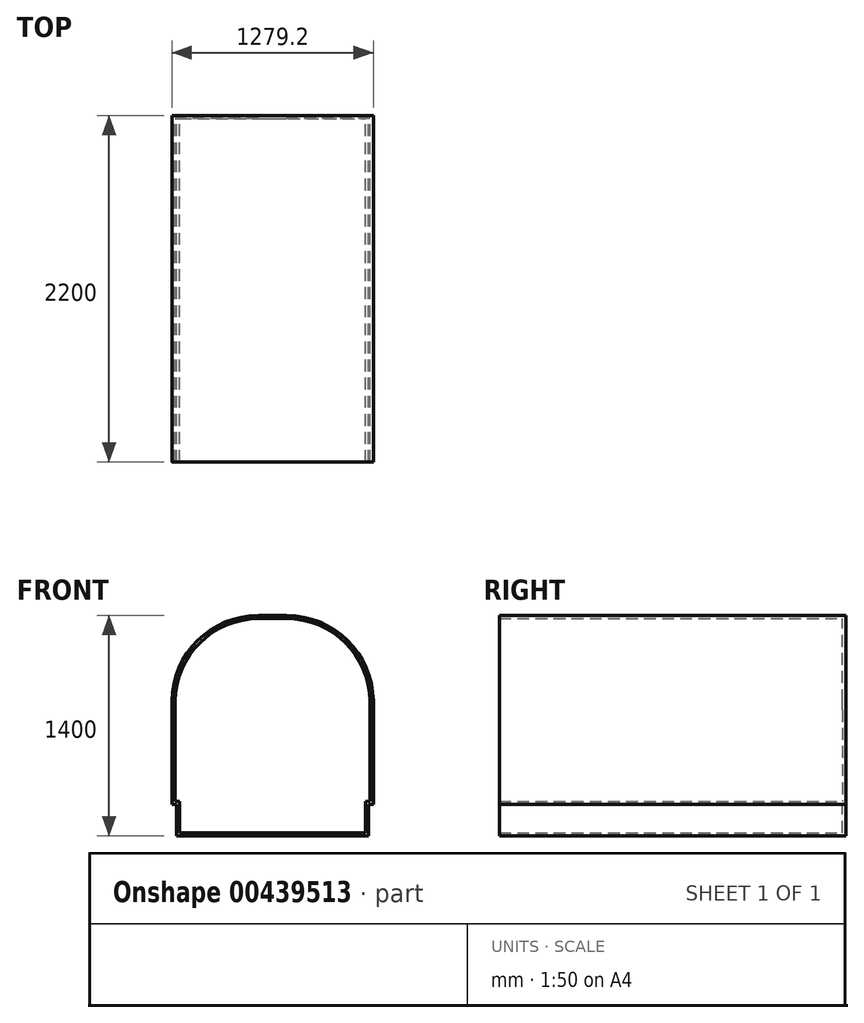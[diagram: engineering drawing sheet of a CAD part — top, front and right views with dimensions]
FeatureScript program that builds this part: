
annotation { "Feature Type Name" : "Feature", "Feature Type Description" : "" }
export const myFeature = defineFeature(function(context is Context, id is Id, definition is map)
    precondition{}
    {
        {
            var Q0;
            Q0=qCreatedBy(makeId("Front.planeOp"),FACE);
            var sketch = newSketch(context, id + "F0", { "sketchPlane" : qUnion([Q0])});
            skLineSegment(sketch, "E0", {"start": v(-609.6, 0) * mm, "end": v(609.6, 0) * mm});
            skLineSegment(sketch, "E1", {"start": v(-609.6, 0) * mm, "end": v(-609.6, 300) * mm});
            skLineSegment(sketch, "E2", {"start": v(609.6, 0) * mm, "end": v(609.6, 300) * mm});
            skLineSegment(sketch, "E3", {"start": v(-609.6, 300) * mm, "end": v(609.6, 300) * mm, "construction": true});
            skLineSegment(sketch, "E4", {"start": v(-89.29, 1400) * mm, "end": v(89.29, 1400) * mm});
            skLineSegment(sketch, "E5", {"start": v(0, 0) * mm, "end": v(0, 1400) * mm, "construction": true});
            skLineSegment(sketch, "E6", {"start": v(-1109.6, 300) * mm, "end": v(-309.6, 300) * mm, "construction": true});
            skLineSegment(sketch, "E7", {"start": v(-639.6, 800) * mm, "end": v(-639.6, 200) * mm});
            skLineSegment(sketch, "E8.MirrorCS", {"start": v(639.6, 800) * mm, "end": v(639.6, 200) * mm});
            skArc(sketch, "E9", {"start": v(-639.6, 800) * mm, "mid": v(-639.51, 828.42) * mm, "end": v(-639.25, 856.85) * mm});
            skArc(sketch, "E10", {"start": v(639.6, 800) * mm, "mid": v(639.51, 828.42) * mm, "end": v(639.25, 856.85) * mm});
            skPoint(sketch, "E11.visualSharp", {"position": v(-600, 1400) * mm});
            skArc(sketch, "E11.filletArc", {"start": v(-89.29, 1400) * mm, "mid": v(-475.77, 1241.32) * mm, "end": v(-639.25, 856.85) * mm});
            skPoint(sketch, "E12.visualSharp", {"position": v(600, 1400) * mm});
            skArc(sketch, "E12.filletArc", {"start": v(639.25, 856.85) * mm, "mid": v(475.77, 1241.32) * mm, "end": v(89.29, 1400) * mm});
            skLineSegment(sketch, "E13", {"start": v(-639.6, 200) * mm, "end": v(-609.6, 200) * mm});
            skLineSegment(sketch, "E14", {"start": v(639.6, 200) * mm, "end": v(609.6, 200) * mm});
            skCircle(sketch, "E15", {"center": v(-405.52, 1300) * mm, "radius": 1124.63 * mm, "construction": true});
            skLineSegment(sketch, "E16", {"start": v(-1109.6, 300) * mm, "end": v(-1109.6, 423.04) * mm});
            skSolve(sketch);
        }
        {
            var Q0;
            Q0=qSketchRegion(id+"F0",true);
            extrude(context, id + "F1", {"entities" : qUnion([Q0]), "depth" : 2200 * mm});
        }
        {
            var Q0;
            Q0=makeQuery(id+"F1.opExtrude","CAP_FACE",FACE,{"disambiguationData":[OSD([sQuery(id+"F0.wireOp",EDGE,"E0"),sQuery(id+"F0.wireOp",EDGE,"E1"),sQuery(id+"F0.wireOp",EDGE,"E2"),sQuery(id+"F0.wireOp",EDGE,"E4"),sQuery(id+"F0.wireOp",EDGE,"3df741bf-00aa-4e76-a0c7-f7b0b77aa621"),sQuery(id+"F0.wireOp",EDGE,"6fed6d78-777c-4dff-9b01-a5f90d519f82"),sQuery(id+"F0.wireOp",EDGE,"bca19fb2-4df8-4f06-bd02-8d9c50e149b9"),sQuery(id+"F0.wireOp",EDGE,"E7"),sQuery(id+"F0.wireOp",EDGE,"c597f7f8-ba4b-4117-8ee7-06938dc063410.MirrorCS"),sQuery(id+"F0.wireOp",EDGE,"E8.MirrorCS"),sQuery(id+"F0.wireOp",EDGE,"3b7a2c63-392d-4415-9d25-b7fee838797f"),sQuery(id+"F0.wireOp",EDGE,"1df09146-72df-46f6-88e9-4f3c2d156cca")])],"isStart":false});
            shell(context, id + "F2", {"entities" : qUnion([Q0]), "thickness" : 20 * mm});
        }
    });
